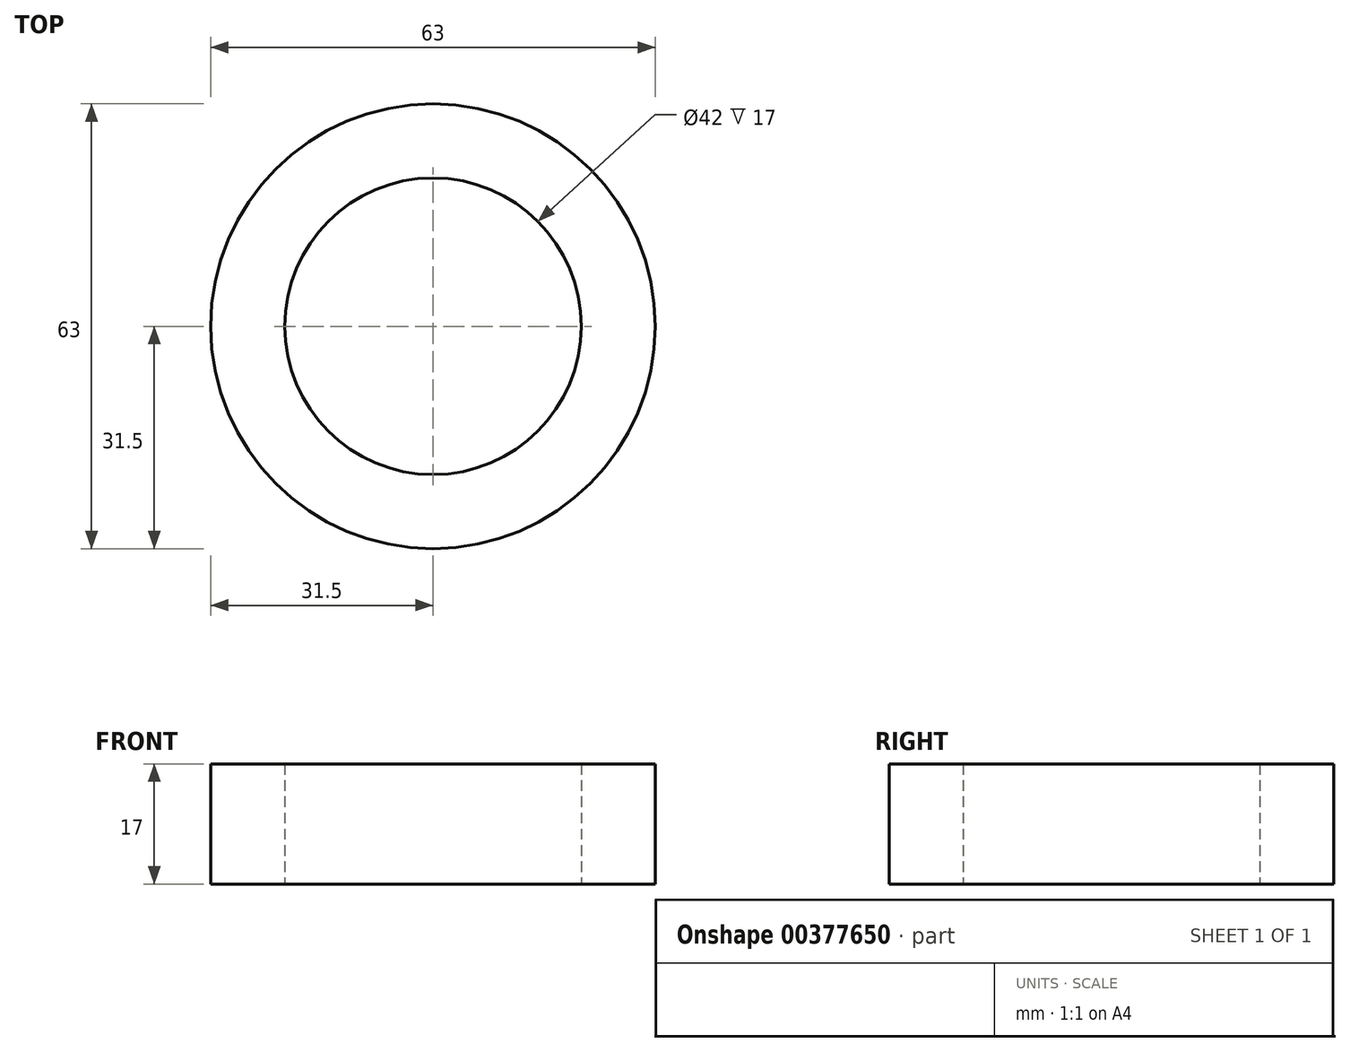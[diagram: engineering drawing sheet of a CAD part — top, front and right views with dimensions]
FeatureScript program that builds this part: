
annotation { "Feature Type Name" : "Feature", "Feature Type Description" : "" }
export const myFeature = defineFeature(function(context is Context, id is Id, definition is map)
    precondition{}
    {
        {
            var Q0;
            Q0=qCreatedBy(makeId("Top.planeOp"),FACE);
            var sketch = newSketch(context, id + "F0", { "sketchPlane" : qUnion([Q0])});
            skCircle(sketch, "E0", {"center": v(0, 0) * mm, "radius": 21 * mm});
            skCircle(sketch, "E1", {"center": v(0, 0) * mm, "radius": 31.5 * mm});
            skSolve(sketch);
        }
        {
            var Q0;
            Q0=makeQuery(id+"F0.imprint","IMPRINT",FACE,{"disambiguationData":[TD([[makeQuery(id+"F0.imprint","IMPRINT",EDGE,{"derivedFrom":sQuery(id+"F0.wireOp",EDGE,"E0")}),-1.0]])]});
            extrude(context, id + "F1", {"entities" : qUnion([Q0]), "depth" : 17 * mm});
        }
    });
